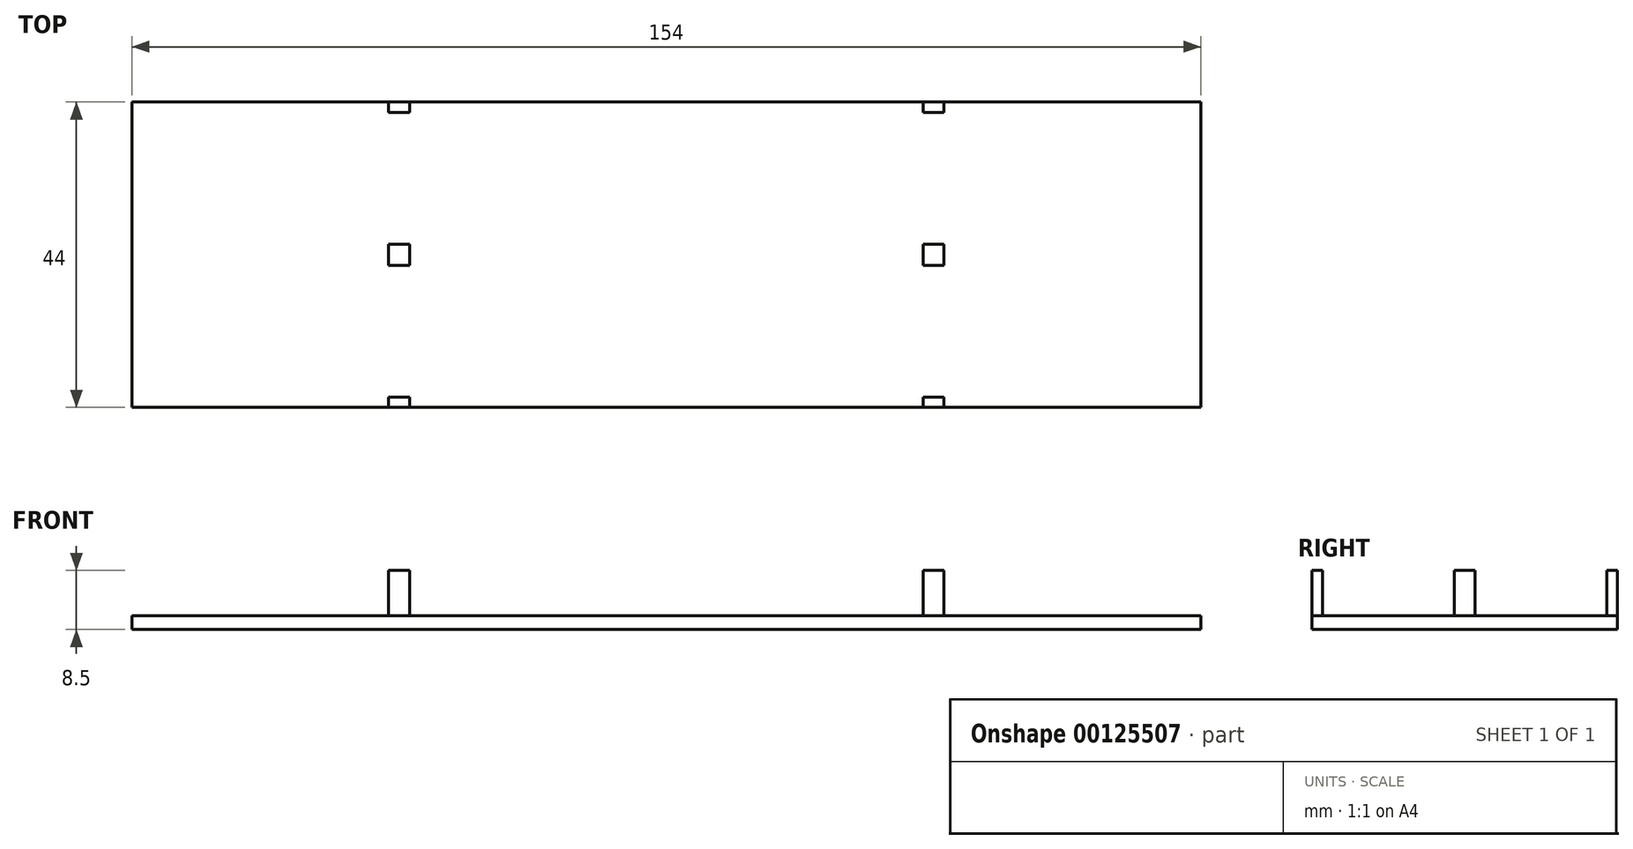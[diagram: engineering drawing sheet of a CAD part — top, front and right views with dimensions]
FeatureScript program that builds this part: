
annotation { "Feature Type Name" : "Feature", "Feature Type Description" : "" }
export const myFeature = defineFeature(function(context is Context, id is Id, definition is map)
    precondition{}
    {
        {
            var Q0;
            Q0=qCreatedBy(makeId("Top.planeOp"),FACE);
            var sketch = newSketch(context, id + "F0", { "sketchPlane" : qUnion([Q0])});
            skLineSegment(sketch, "E0.bottom", {"start": v(-77, -22) * mm, "end": v(77, -22) * mm});
            skLineSegment(sketch, "E0.top", {"start": v(-77, 22) * mm, "end": v(77, 22) * mm});
            skLineSegment(sketch, "E0.left", {"start": v(-77, -22) * mm, "end": v(-77, 22) * mm});
            skLineSegment(sketch, "E0.right", {"start": v(77, -22) * mm, "end": v(77, 22) * mm});
            skPoint(sketch, "E0.middle", {"position": v(0, 0) * mm});
            skLineSegment(sketch, "E1", {"start": v(0, 22) * mm, "end": v(0, -22) * mm, "construction": true});
            skLineSegment(sketch, "E2", {"start": v(-77, 0) * mm, "end": v(77, 0) * mm, "construction": true});
            skLineSegment(sketch, "E3.bottom", {"start": v(37, 1.5) * mm, "end": v(40, 1.5) * mm});
            skLineSegment(sketch, "E3.top", {"start": v(37, -1.5) * mm, "end": v(40, -1.5) * mm});
            skLineSegment(sketch, "E3.left", {"start": v(37, 1.5) * mm, "end": v(37, -1.5) * mm});
            skLineSegment(sketch, "E3.right", {"start": v(40, 1.5) * mm, "end": v(40, -1.5) * mm});
            skPoint(sketch, "E3.middle", {"position": v(38.5, 0) * mm});
            skLineSegment(sketch, "E4", {"start": v(37, 22) * mm, "end": v(37, 20.5) * mm});
            skLineSegment(sketch, "E5", {"start": v(37, 20.5) * mm, "end": v(40, 20.5) * mm});
            skLineSegment(sketch, "E6", {"start": v(40, 20.5) * mm, "end": v(40, 22) * mm});
            skLineSegment(sketch, "E7.MirrorCS", {"start": v(37, -22) * mm, "end": v(37, -20.5) * mm});
            skLineSegment(sketch, "E8.MirrorCS", {"start": v(37, -20.5) * mm, "end": v(40, -20.5) * mm});
            skLineSegment(sketch, "E9.MirrorCS", {"start": v(40, -20.5) * mm, "end": v(40, -22) * mm});
            skLineSegment(sketch, "E10.MirrorCS", {"start": v(-37, 22) * mm, "end": v(-37, 20.5) * mm});
            skLineSegment(sketch, "E11.MirrorCS", {"start": v(-37, 20.5) * mm, "end": v(-40, 20.5) * mm});
            skLineSegment(sketch, "E12.MirrorCS", {"start": v(-40, 20.5) * mm, "end": v(-40, 22) * mm});
            skLineSegment(sketch, "E13.MirrorCS", {"start": v(-37, 1.5) * mm, "end": v(-40, 1.5) * mm});
            skLineSegment(sketch, "E14.MirrorCS", {"start": v(-37, 1.5) * mm, "end": v(-37, -1.5) * mm});
            skLineSegment(sketch, "E15.MirrorCS", {"start": v(-37, -1.5) * mm, "end": v(-40, -1.5) * mm});
            skLineSegment(sketch, "E16.MirrorCS", {"start": v(-40, 1.5) * mm, "end": v(-40, -1.5) * mm});
            skLineSegment(sketch, "E17.MirrorCS", {"start": v(-37, -20.5) * mm, "end": v(-40, -20.5) * mm});
            skLineSegment(sketch, "E18.MirrorCS", {"start": v(-37, -22) * mm, "end": v(-37, -20.5) * mm});
            skLineSegment(sketch, "E19.MirrorCS", {"start": v(-40, -20.5) * mm, "end": v(-40, -22) * mm});
            skPoint(sketch, "E20", {"position": v(38.5, 11) * mm});
            skPoint(sketch, "E21.MirrorP", {"position": v(-38.5, 11) * mm});
            skPoint(sketch, "E22.MirrorP", {"position": v(-38.5, -11) * mm});
            skPoint(sketch, "E23.MirrorP", {"position": v(38.5, -11) * mm});
            skSolve(sketch);
        }
        {
            var Q0;
            Q0=makeQuery(id+"F0.imprint","IMPRINT",FACE,{"disambiguationData":[TD([[makeQuery(id+"F0.imprint","IMPRINT",EDGE,{"derivedFrom":sQuery(id+"F0.wireOp",EDGE,"E13.MirrorCS")}),1.0]])]});
            var Q1;
            Q1=makeQuery(id+"F0.imprint","IMPRINT",FACE,{"disambiguationData":[TD([[makeQuery(id+"F0.imprint","IMPRINT",EDGE,{"derivedFrom":sQuery(id+"F0.wireOp",EDGE,"E17.MirrorCS")}),1.0]])]});
            var Q2;
            {var subQ0=sQuery(id+"F0.wireOp",EDGE,"E4");Q2=makeQuery(id+"F0.imprint","IMPRINT",FACE,{"disambiguationData":[TD([[makeQuery(id+"F0.imprint","IMPRINT",EDGE,{"derivedFrom":subQ0}),1.0]])]});}
            var Q3;
            {var subQ0=sQuery(id+"F0.wireOp",EDGE,"E10.MirrorCS");Q3=makeQuery(id+"F0.imprint","IMPRINT",FACE,{"disambiguationData":[TD([[makeQuery(id+"F0.imprint","IMPRINT",EDGE,{"derivedFrom":subQ0}),-1.0]])]});}
            var Q4;
            Q4=makeQuery(id+"F0.imprint","IMPRINT",FACE,{"disambiguationData":[TD([[makeQuery(id+"F0.imprint","IMPRINT",EDGE,{"derivedFrom":sQuery(id+"F0.wireOp",EDGE,"E3.bottom")}),-1.0]])]});
            var Q5;
            {var subQ0=sQuery(id+"F0.wireOp",EDGE,"E7.MirrorCS");Q5=makeQuery(id+"F0.imprint","IMPRINT",FACE,{"disambiguationData":[TD([[makeQuery(id+"F0.imprint","IMPRINT",EDGE,{"derivedFrom":subQ0}),-1.0]])]});}
            extrude(context, id + "F1", {"entities" : qUnion([Q0, Q1, Q2, Q3, Q4, Q5]), "depth" : 1.5 * mm, "hasSecondDirection" : true, "secondDirectionOppositeDirection" : true, "secondDirectionDepth" : 5 * mm});
        }
        {
            var Q0;
            Q0=makeQuery(id+"F1.opExtrude","CAP_FACE",FACE,{"disambiguationData":[OSD([sQuery(id+"F0.wireOp",EDGE,"E13.MirrorCS"),sQuery(id+"F0.wireOp",EDGE,"E14.MirrorCS"),sQuery(id+"F0.wireOp",EDGE,"E15.MirrorCS"),sQuery(id+"F0.wireOp",EDGE,"E16.MirrorCS")])],"isStart":true});
            var sketch = newSketch(context, id + "F2", { "sketchPlane" : qUnion([Q0])});
            skLineSegment(sketch, "E24.0", {"start": v(-77, 22) * mm, "end": v(77, 22) * mm});
            skLineSegment(sketch, "E25.0", {"start": v(-77, 22) * mm, "end": v(-77, -22) * mm});
            skLineSegment(sketch, "E26.0", {"start": v(-77, -22) * mm, "end": v(77, -22) * mm});
            skLineSegment(sketch, "E27.0", {"start": v(77, 22) * mm, "end": v(77, -22) * mm});
            skLineSegment(sketch, "E28.0", {"start": v(-80, 25) * mm, "end": v(80, 25) * mm});
            skLineSegment(sketch, "E28.1", {"start": v(-80, 25) * mm, "end": v(-80, -25) * mm});
            skLineSegment(sketch, "E28.2", {"start": v(-80, -25) * mm, "end": v(80, -25) * mm});
            skLineSegment(sketch, "E28.3", {"start": v(80, 25) * mm, "end": v(80, -25) * mm});
            skSolve(sketch);
        }
        {
            var Q0;
            Q0=makeQuery(id+"F2.imprint","IMPRINT",FACE,{"disambiguationData":[TD([[makeQuery(id+"F2.imprint","IMPRINT",EDGE,{"derivedFrom":sQuery(id+"F2.wireOp",EDGE,"E24.0")}),-1.0]])]});
            var Q1;
            Q1=makeQuery(id+"F2.imprint","IMPRINT",FACE,{"disambiguationData":[TD([[makeQuery(id+"F2.imprint","IMPRINT",EDGE,{"derivedFrom":makeQuery(id+"F1.opExtrude","CAP_EDGE",EDGE,{"disambiguationData":[OSD([sQuery(id+"F0.wireOp",EDGE,"E13.MirrorCS")])],"isStart":true})}),-1.0]])]});
            extrude(context, id + "F3", {"entities" : qUnion([Q0, Q1]), "depth" : 2 * mm});
        }
    });
